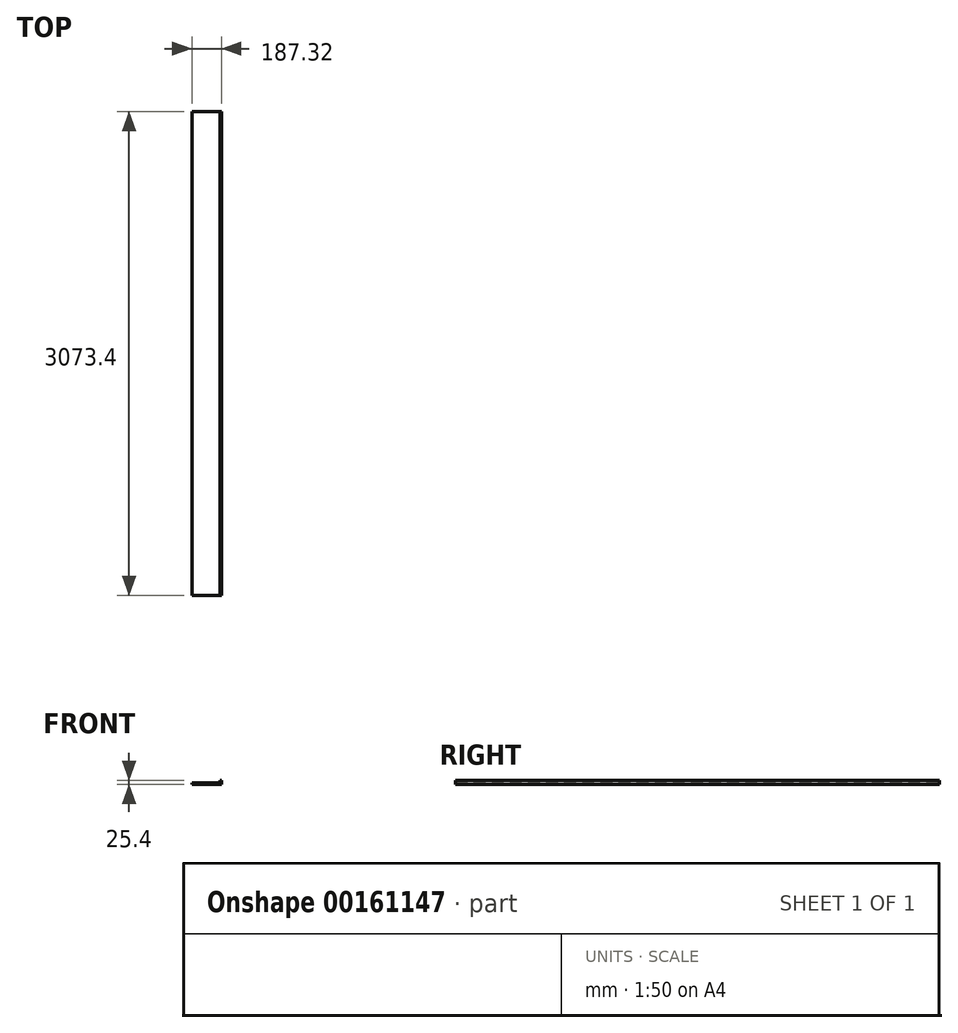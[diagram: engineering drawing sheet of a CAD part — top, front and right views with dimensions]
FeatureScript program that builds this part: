
annotation { "Feature Type Name" : "Feature", "Feature Type Description" : "" }
export const myFeature = defineFeature(function(context is Context, id is Id, definition is map)
    precondition{}
    {
        {
            var Q0;
            Q0=qCreatedBy(makeId("Front.planeOp"),FACE);
            var sketch = newSketch(context, id + "F0", { "sketchPlane" : qUnion([Q0])});
            skLineSegment(sketch, "E0.bottom", {"start": v(0, 0) * mm, "end": v(187.33, 0) * mm});
            skLineSegment(sketch, "E0.top", {"start": v(0, 9.53) * mm, "end": v(177.8, 9.53) * mm});
            skLineSegment(sketch, "E0.left", {"start": v(0, 0) * mm, "end": v(0, 9.53) * mm});
            skLineSegment(sketch, "E0.right", {"start": v(187.33, 0) * mm, "end": v(187.33, 9.53) * mm});
            skLineSegment(sketch, "E1.bottom", {"start": v(187.33, 0) * mm, "end": v(177.8, 0) * mm});
            skLineSegment(sketch, "E1.top", {"start": v(187.33, 25.4) * mm, "end": v(177.8, 25.4) * mm});
            skLineSegment(sketch, "E1.left", {"start": v(187.33, 0) * mm, "end": v(187.33, 25.4) * mm});
            skLineSegment(sketch, "E1.right", {"start": v(177.8, 9.53) * mm, "end": v(177.8, 25.4) * mm});
            skSolve(sketch);
        }
        {
            var Q0;
            Q0=qSketchRegion(id+"F0",true);
            extrude(context, id + "F1", {"entities" : qUnion([Q0]), "depth" : 3073.4 * mm});
        }
    });
